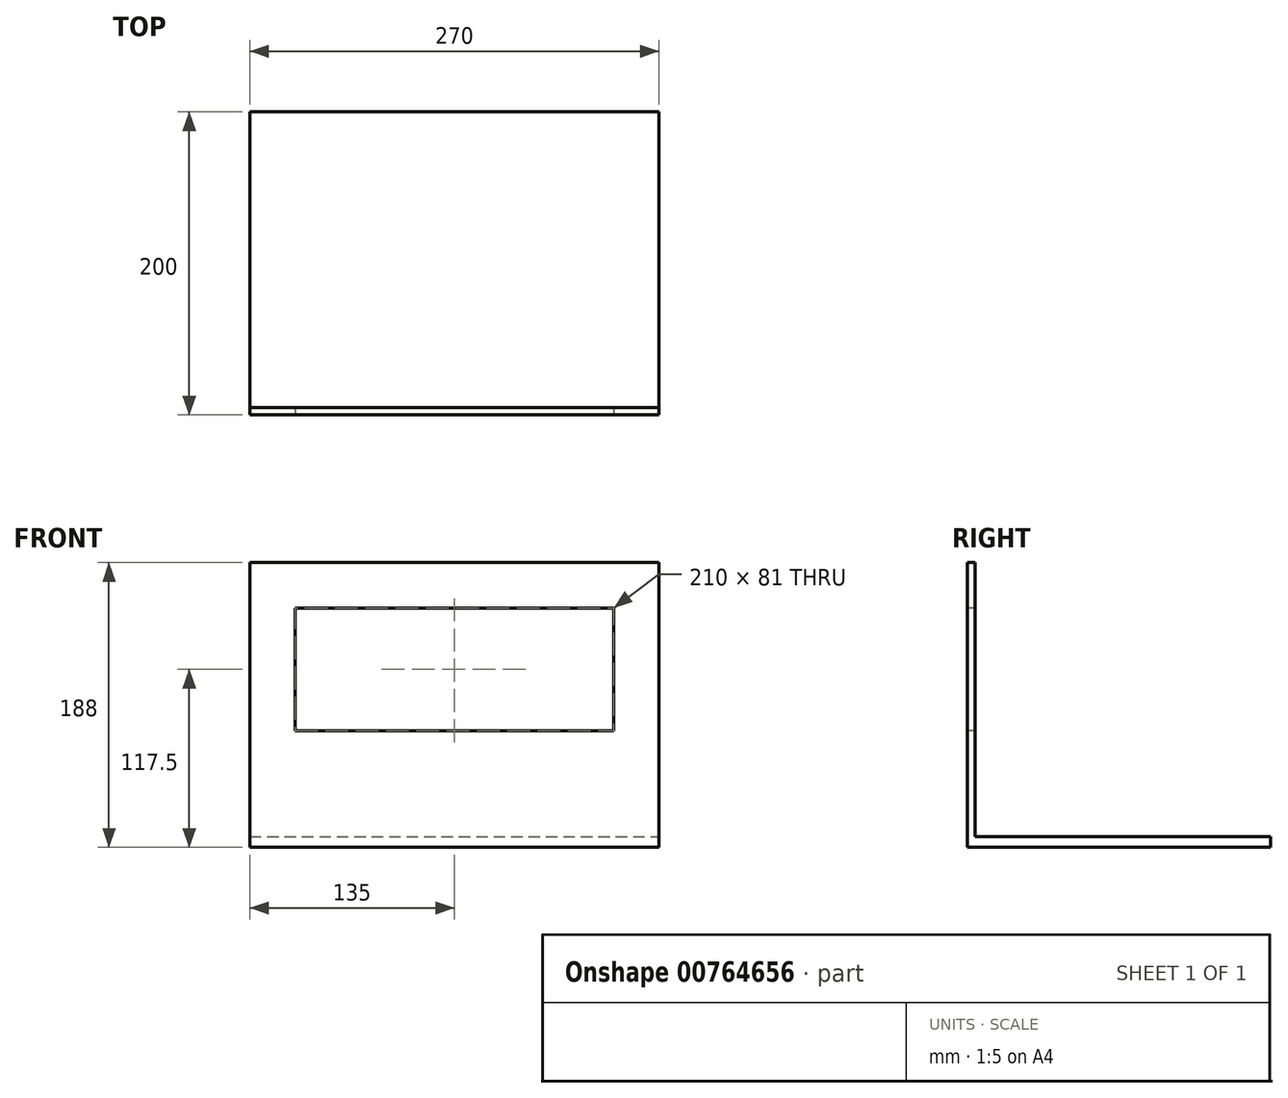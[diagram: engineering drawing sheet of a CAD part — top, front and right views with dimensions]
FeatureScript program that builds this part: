
annotation { "Feature Type Name" : "Feature", "Feature Type Description" : "" }
export const myFeature = defineFeature(function(context is Context, id is Id, definition is map)
    precondition{}
    {
        {
            var Q0;
            Q0=qCreatedBy(makeId("Front.planeOp"),FACE);
            var sketch = newSketch(context, id + "F0", { "sketchPlane" : qUnion([Q0])});
            skLineSegment(sketch, "E0.bottom", {"start": v(0, 0) * mm, "end": v(210, 0) * mm});
            skLineSegment(sketch, "E0.top", {"start": v(0, 81) * mm, "end": v(210, 81) * mm});
            skLineSegment(sketch, "E0.left", {"start": v(0, 0) * mm, "end": v(0, 81) * mm});
            skLineSegment(sketch, "E0.right", {"start": v(210, 0) * mm, "end": v(210, 81) * mm});
            skLineSegment(sketch, "E1.bottom", {"start": v(-30, -70) * mm, "end": v(240, -70) * mm});
            skLineSegment(sketch, "E1.top", {"start": v(-30, 111) * mm, "end": v(240, 111) * mm});
            skLineSegment(sketch, "E1.left", {"start": v(-30, -70) * mm, "end": v(-30, 111) * mm});
            skLineSegment(sketch, "E1.right", {"start": v(240, -70) * mm, "end": v(240, 111) * mm});
            skLineSegment(sketch, "E2.top", {"start": v(-30, -77) * mm, "end": v(240, -77) * mm});
            skLineSegment(sketch, "E2.left", {"start": v(-30, -70) * mm, "end": v(-30, -77) * mm});
            skLineSegment(sketch, "E2.right", {"start": v(240, -70) * mm, "end": v(240, -77) * mm});
            skSolve(sketch);
        }
        {
            var Q0;
            Q0=makeQuery(id+"F0.imprint","IMPRINT",FACE,{"disambiguationData":[TD([[makeQuery(id+"F0.imprint","IMPRINT",EDGE,{"derivedFrom":sQuery(id+"F0.wireOp",EDGE,"E0.bottom")}),-1.0]])]});
            extrude(context, id + "F1", {"entities" : qUnion([Q0]), "depth" : -5 * mm, "offsetDistance" : 25 * mm});
        }
        {
            var Q0;
            Q0=makeQuery(id+"F0.imprint","IMPRINT",FACE,{"disambiguationData":[TD([[makeQuery(id+"F0.imprint","IMPRINT",EDGE,{"derivedFrom":sQuery(id+"F0.wireOp",EDGE,"E1.bottom")}),-1.0]])]});
            extrude(context, id + "F2", {"entities" : qUnion([Q0]), "operationType" : NewBodyOperationType.ADD, "depth" : -200 * mm, "offsetDistance" : 25 * mm});
        }
    });
